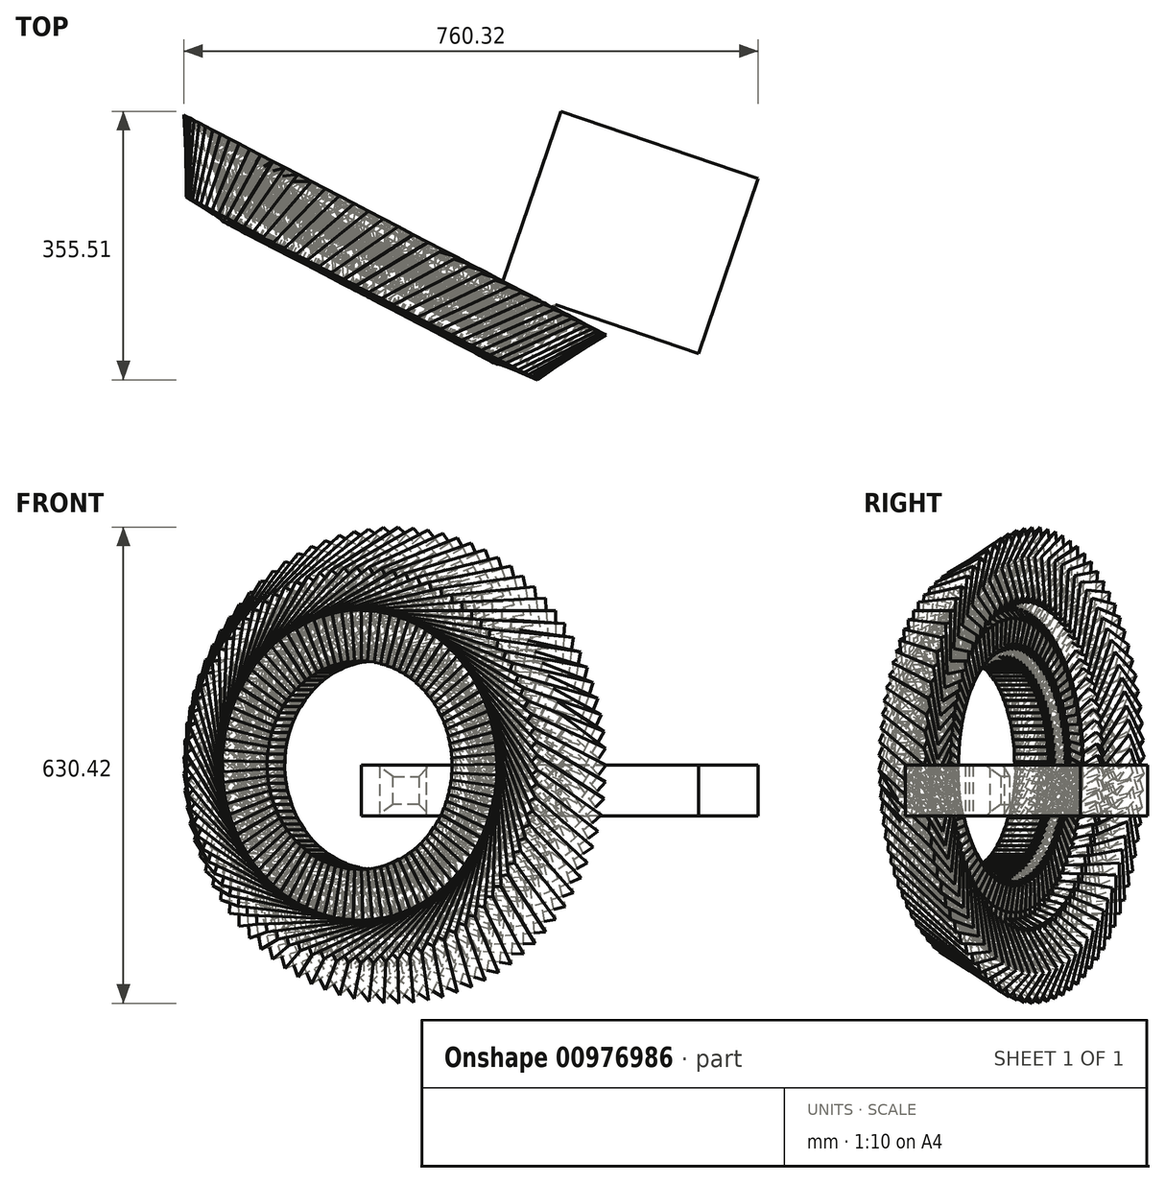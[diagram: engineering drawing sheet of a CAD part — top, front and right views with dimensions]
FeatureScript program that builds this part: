
annotation { "Feature Type Name" : "Feature", "Feature Type Description" : "" }
export const myFeature = defineFeature(function(context is Context, id is Id, definition is map)
    precondition{}
    {
        {
            var Q0;
            Q0=qCreatedBy(makeId("Top.planeOp"),FACE);
            var sketch = newSketch(context, id + "F0", { "sketchPlane" : qUnion([Q0])});
            skLineSegment(sketch, "E0", {"start": v(-42.6, 38.98) * mm, "end": v(50.44, 38.98) * mm});
            skLineSegment(sketch, "E1", {"start": v(50.44, 38.98) * mm, "end": v(56.6, -35.7) * mm});
            skLineSegment(sketch, "E2", {"start": v(56.6, -35.7) * mm, "end": v(-44.12, -50.03) * mm});
            skLineSegment(sketch, "E3", {"start": v(-44.12, -50.03) * mm, "end": v(-42.6, 38.98) * mm});
            skLineSegment(sketch, "E4", {"start": v(-99.7, 27.36) * mm, "end": v(127.46, -50.28) * mm});
            skLineSegment(sketch, "E5", {"start": v(127.46, -50.28) * mm, "end": v(16.6, -99.33) * mm});
            skLineSegment(sketch, "E6", {"start": v(16.6, -99.33) * mm, "end": v(-129.82, -30.46) * mm});
            skLineSegment(sketch, "E7", {"start": v(-129.82, -30.46) * mm, "end": v(-99.7, 27.36) * mm});
            skSolve(sketch);
        }
        {
            var Q0;
            {var subQ4=sQuery(id+"F0.wireOp",EDGE,"E2");Q0=makeQuery(id+"F0.imprint","IMPRINT",FACE,{"disambiguationData":[TD([[makeQuery(id+"F0.imprint","IMPRINT",EDGE,{"derivedFrom":subQ4}),1.0]])]});}
            extrude(context, id + "F1", {"entities" : qUnion([Q0]), "depth" : 66.95 * mm, "offsetDistance" : 25 * mm});
        }
        {
            var Q0;
            {var subQ0=sQuery(id+"F0.wireOp",EDGE,"E4");Q0=makeQuery(id+"F1.opExtrude","SWEPT_FACE",FACE,{"disambiguationData":[OSD([subQ0]),TDD([makeQuery(id+"F0.imprint","IMPRINT",EDGE,{"disambiguationData":[TD([[makeQuery(id+"F0.imprint","INTERSECT",VERTEX,{"derivedFrom":[subQ0,sQuery(id+"F0.wireOp",EDGE,"E7")]}),-1.0]])],"derivedFrom":subQ0})])]});}
            chamfer(context, id + "F2", {"entities" : qUnion([Q0]), "width" : 15 * mm, "tangentPropagation" : true});
        }
        {
            var Q0;
            Q0=makeQuery(id+"F1.opExtrude","SWEPT_BODY",BODY,{"disambiguationData":[OSD([sQuery(id+"F0.wireOp",EDGE,"E1"),sQuery(id+"F0.wireOp",EDGE,"E2"),sQuery(id+"F0.wireOp",EDGE,"E3"),sQuery(id+"F0.wireOp",EDGE,"E4"),sQuery(id+"F0.wireOp",EDGE,"E5"),sQuery(id+"F0.wireOp",EDGE,"E6"),sQuery(id+"F0.wireOp",EDGE,"E7")])]});
            transform(context, id + "F3", {"entities" : qUnion([Q0]), "transformType" : TransformType.TRANSLATION_3D, "dx" : 0 * mm, "dy" : -5.22 * mm, "dz" : 204.73 * mm, "makeCopy" : true});
        }
        {
            var Q0;
            Q0=makeQuery(id+"F3.opPattern","COPY",BODY,{"derivedFrom":makeQuery(id+"F1.opExtrude","SWEPT_BODY",BODY,{"disambiguationData":[OSD([sQuery(id+"F0.wireOp",EDGE,"E1"),sQuery(id+"F0.wireOp",EDGE,"E2"),sQuery(id+"F0.wireOp",EDGE,"E3"),sQuery(id+"F0.wireOp",EDGE,"E4"),sQuery(id+"F0.wireOp",EDGE,"E5"),sQuery(id+"F0.wireOp",EDGE,"E6"),sQuery(id+"F0.wireOp",EDGE,"E7")])]}),"instanceName":"1"});
            var Q1;
            Q1=makeQuery(id+"F1.opExtrude","CAP_EDGE",EDGE,{"disambiguationData":[OSD([sQuery(id+"F0.wireOp",EDGE,"E7")])],"isStart":false});
            circularPattern(context, id + "F4", {"entities" : qUnion([Q0]), "axis" : qUnion([Q1]), "angle" : 360 * degree, "instanceCount" : 89, "equalSpace" : true});
        }
        {
            var Q0;
            {var subQ0=sQuery(id+"F0.wireOp",EDGE,"E4");Q0=makeQuery(id+"F1.opExtrude","SWEPT_FACE",FACE,{"disambiguationData":[OSD([subQ0]),TDD([makeQuery(id+"F0.imprint","IMPRINT",EDGE,{"disambiguationData":[TD([[makeQuery(id+"F0.imprint","INTERSECT",VERTEX,{"derivedFrom":[subQ0,sQuery(id+"F0.wireOp",EDGE,"E5")]}),1.0]])],"derivedFrom":subQ0})])]});}
            extrude(context, id + "F5", {"entities" : qUnion([Q0]), "operationType" : NewBodyOperationType.ADD, "depth" : 244.5 * mm, "offsetDistance" : 25 * mm});
        }
        {
            var Q0;
            Q0=makeQuery(id+"F5.opExtrude","SWEPT_FACE",FACE,{"disambiguationData":[OSD([sQuery(id+"F0.wireOp",EDGE,"E4"),sQuery(id+"F0.wireOp",EDGE,"E5")])]});
            extrude(context, id + "F6", {"entities" : qUnion([Q0]), "operationType" : NewBodyOperationType.ADD, "depth" : 199.93 * mm, "offsetDistance" : 25 * mm});
        }
    });
